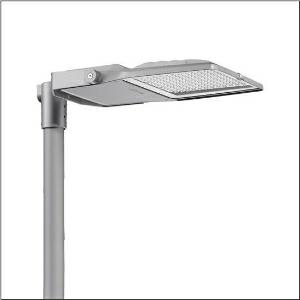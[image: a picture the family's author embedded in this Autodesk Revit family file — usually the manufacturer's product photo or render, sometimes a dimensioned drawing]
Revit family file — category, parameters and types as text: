
# Revit family: floodlight_fl_21_midi___pl33t_5xa7785f2f3a_cf02
name_source: partatom
category: Lighting Fixtures
units: mm (PartAtom-declared; Revit-internal decimal feet)

## family parameters
Cut with Voids When Loaded = No
Host = Face
Light Source = No
Part Type = Normal
Room Calculation Point = No
Round Connector Dimension = Use Diameter
Shared = No

## types (1)
- --- (1 x LED, 35340 lm, 271.6 W, 3000K)
    Apparent Load = 272 VA
    CIE Flux Codes = 26 75 99 100 100
    Color Rendering = 70
    Color Temperature = 3000K
    Default Elevation = 1800 mm
    Description = Floodlight FL 21 midi, floodlight, primary light control with lens, of PMMA, primary optical cover: protective disc, of toughened safety glass, transparent, light distribution: PL33T, light emission: direct distribution, installation type: surface-mounted, LED, High Power LED, rated luminous flux: 35.340lm, luminous efficacy: 130lm/W, light colour: 730, colour temperature: 3000K, control gear: Smart Interface (Zhaga), control: flexible luminous flux parameterisation, time-dependent luminous flux control, constant luminous flux control, overheat protection, pre-setting: logarithmic dimming characteristic, with terminal, 6-pole, mains connection: 220..240V, AC, 50/60Hz, start of lifetime: 272W, end of service life: 287W, reduction: 123W, luminaire housing, of diecast aluminium, powder-coated, Siteco® metallic grey (DB 702S), corrosivity category C5 mid according to DIN EN ISO 12944, suitable for swimming pools, chlorine-resistant, sealing non-destructively replaceable, please order mast flange separately, mast bracket, of steel, galvanised, powder-coated, Siteco® metallic grey (DB 702S), Smart Interface above, protection rating (complete): IP66, insulation class (complete): insulation class II (safety insulation), certification: CE, ENEC, VDE, protection symbol: D, impact resistance: IK08, permissible operating ambient temperature: -40..+40°C, permissible operating ambient temperature for outdoor applications: -40..+50°C, standard: DIN EN 12944, LABS conformity tested according to VDMA 24364:2018-05, packaging unit: 1 piece

Light Distribution: PL33T
    Height = 76 mm
    Lamp = 1 x LED
    Lamp Light Flux = 35340 lm
    Lamp Power = 271.6 W
    Lamp count = 1
    Length = 657 mm
    Luminous efficacy = 130 lm/W
    Manufacturer = Siteco
    ModVariant = No
    Model = 5XA7785F2F3A
    Number of Poles = 1
    OnlyDefault = Yes
    Power Factor = 1
    Product Name = Floodlight FL 21 midi | PL33T
    Product group = floodlight | pylon annexe
    ProductGroupID = 6200
    Protection Class = Protection class II
    Protection Degree = IP 66
    RLX_Detail_Level = 1
    RLX_Emergency_Light_Flux = 0 lm
    RLX_Emergency_Type = 0
    RLX_Emergency_Type_DB = No
    RlxData = <blob elided: 153729 chars, md5=d18a5650>
    Socket = socket
    Standby Power = 0 W
    System Light Flux = 35340 lm
    System Power = 272 W
    Type Comments = factory setting: luminous flux: 100 % | dim-lin: 254 | 620 mA
    Type Image = l_1007123.jpg
    URL = http://relux.com
    VarID = @adj_150468
    Voltage = 0 V
    Weight = 0.00 kg
    Width = 442 mm

## geometry (parser evidence)
native form markers: Blend x4, Sweep x14
no freeform markers — native parametric forms only
